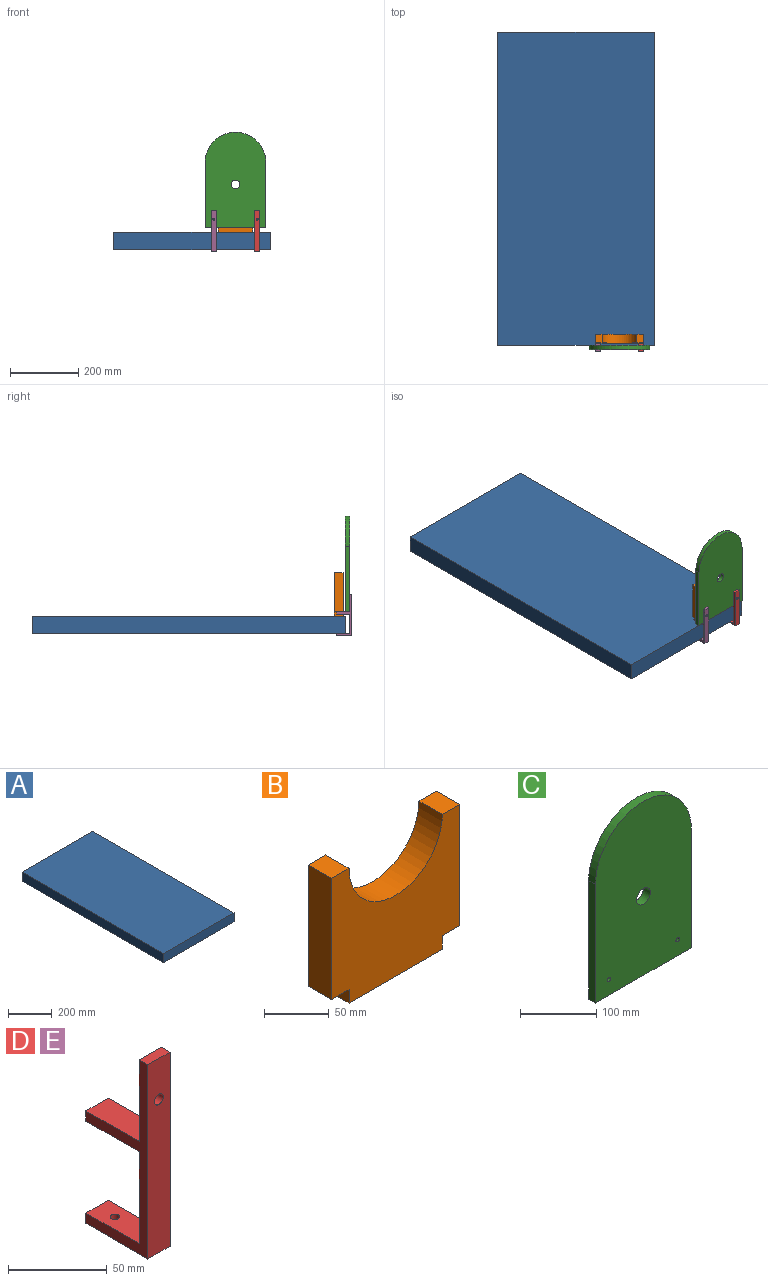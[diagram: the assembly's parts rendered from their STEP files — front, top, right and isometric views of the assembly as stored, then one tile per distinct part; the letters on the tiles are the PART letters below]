
ASSEMBLY  parts=5 mates=4
PART A: 6 faces, bbox 457.2x914.4x50.8 mm
  f0: plane 914.4x50.8mm, normal (-1,0,0), area 46451.5mm2, adj f1,f3,f4,f5
  f1: plane 457.2x50.8mm, normal (0,-1,0), area 23225.8mm2, adj f0,f2,f4,f5
  f2: plane 914.4x50.8mm, normal (1,0,0), area 46451.5mm2, adj f1,f3,f4,f5
  f3: plane 457.2x50.8mm, normal (0,1,0), area 23225.8mm2, adj f0,f2,f4,f5
  f4: plane 914.4x457.2mm, normal (0,0,1), area 418063.7mm2, adj f0,f1,f2,f3
  f5: plane 914.4x457.2mm, normal (0,0,-1), area 418063.7mm2, adj f0,f1,f2,f3
PART B: 12 faces, bbox 139.7x25.4x127 mm
  f0: cylinder r=50.8mm len=101.6mm, axis (0,1,0), area 4053.7mm2, adj f1,f9,f10,f11
  f1: plane 25.4x19.05mm, normal (0,0,1), area 483.9mm2, adj f0,f2,f10,f11
  f2: plane 114.3x25.4mm, normal (-1,0,0), area 2903.2mm2, adj f1,f3,f10,f11
  f3: plane 25.4x19.05mm, normal (0,0,-1), area 483.9mm2, adj f2,f4,f10,f11
  f4: plane 25.4x12.7mm, normal (-1,0,0), area 322.6mm2, adj f3,f5,f10,f11
  f5: plane 101.6x25.4mm, normal (0,0,-1), area 2580.6mm2, adj f4,f6,f10,f11
  f6: plane 25.4x12.7mm, normal (1,0,0), area 322.6mm2, adj f5,f7,f10,f11
  f7: plane 25.4x19.05mm, normal (0,0,-1), area 483.9mm2, adj f6,f8,f10,f11
  f8: plane 114.3x25.4mm, normal (1,0,0), area 2903.2mm2, adj f7,f9,f10,f11
  f9: plane 25.4x19.05mm, normal (0,0,1), area 483.9mm2, adj f0,f8,f10,f11
  f10: plane 139.7x127mm, normal (0,-1,0), area 13204.4mm2, adj f0,f1,f2,f3,f4,f5,f6,f7
  f11: plane 139.7x127mm, normal (0,1,0), area 13204.4mm2, adj f0,f1,f2,f3,f4,f5,f6,f7
PART C: 9 faces, bbox 177.8x12.7x279.4 mm
  f0: plane 177.8x12.7mm, normal (0,0,-1), area 2258.1mm2, adj f1,f4,f5,f6
  f1: plane 190.5x12.7mm, normal (1,0,0), area 2419.3mm2, adj f0,f2,f5,f6
  f2: cylinder r=88.9mm len=177.8mm, axis (0,1,0), area 3547mm2, adj f1,f4,f5,f6
  f3: cylinder r=12.7mm len=25.4mm, axis (0,1,0), area 1013.4mm2, adj f5,f6
  f4: plane 190.5x12.7mm, normal (-1,0,0), area 2419.3mm2, adj f0,f2,f5,f6
  f5: plane 279.4x177.8mm, normal (0,-1,0), area 45715.2mm2, adj f0,f1,f2,f3,f4,f7,f8
  f6: plane 279.4x177.8mm, normal (0,1,0), area 45715.2mm2, adj f0,f1,f2,f3,f4,f7,f8
  f7: cylinder r=3.17mm len=12.7mm, axis (0,-1,0), area 253.4mm2, adj f5,f6
  f8: cylinder r=3.17mm len=12.7mm, axis (0,-1,0), area 253.4mm2, adj f5,f6
PART D: 14 faces, bbox 15.9x44.5x120.7 mm
  f0: plane 57.15x15.88mm, normal (0,1,0), area 907.3mm2, adj f1,f9,f10,f11
  f1: plane 38.1x15.88mm, normal (0,0,-1), area 604.8mm2, adj f0,f2,f10,f11
  f2: plane 15.88x6.35mm, normal (0,1,0), area 100.8mm2, adj f1,f3,f10,f11
  f3: plane 38.1x15.88mm, normal (0,0,1), area 604.8mm2, adj f2,f4,f10,f11
  f4: plane 50.8x15.88mm, normal (0,1,0), area 774.8mm2, adj f3,f5,f10,f11,f12
  f5: plane 15.88x6.35mm, normal (0,0,1), area 100.8mm2, adj f4,f6,f10,f11
  f6: plane 120.65x15.88mm, normal (0,-1,0), area 1883.6mm2, adj f5,f7,f10,f11,f12
  f7: plane 44.45x15.88mm, normal (0,0,-1), area 687.8mm2, adj f6,f8,f10,f11,f13
  f8: plane 15.88x6.35mm, normal (0,1,0), area 100.8mm2, adj f7,f9,f10,f11
  f9: plane 38.1x15.88mm, normal (0,0,1), area 587mm2, adj f0,f8,f10,f11,f13
  f10: plane 120.65x44.45mm, normal (1,0,0), area 1250mm2, adj f0,f1,f2,f3,f4,f5,f6,f7
  f11: plane 120.65x44.45mm, normal (-1,0,0), area 1250mm2, adj f0,f1,f2,f3,f4,f5,f6,f7
  f12: cylinder r=3.17mm len=6.35mm, axis (0,-1,0), area 126.7mm2, adj f4,f6
  f13: cylinder r=2.38mm len=6.35mm, axis (0,0,1), area 95mm2, adj f7,f9
PART E: same geometry as D
PLACE A t=(-127.11,455.19,-179.76)mm fixed
PLACE B t=(-0.11,29.74,-59.11)mm
PLACE C t=(-0.11,-2.01,23.44)mm
PLACE D t=(63.39,-19.47,-116.26)mm
PLACE E t=(-63.61,-19.47,-116.26)mm
MATE fastened B.f5 <-> A.f4  axis (0,0,-1) through (-0.11,17.04,-128.96)mm
MATE fastened D.f9 <-> A.f5  axis (0,0,1) through (63.39,23.39,-179.76)mm
MATE fastened C.f5 <-> E.f4  axis (0,-1,0) through (-0.11,-14.71,-116.26)mm
MATE fastened D.f4 <-> C.f5  axis (0,1,0) through (63.39,-14.71,-116.26)mm
